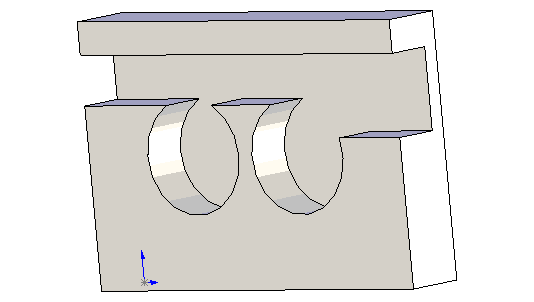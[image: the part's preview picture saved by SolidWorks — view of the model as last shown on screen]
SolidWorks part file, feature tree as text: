
SOLIDWORKS PART (.sldprt)
format: sldprt  version: not decoded by parser v0  size: 99,328 bytes
history: native  units: mm
features: sketch x4, cut_extrude x3, extrude x1 (+11 scaffold rows collapsed)
feature tree (19):
  scaffold x11  (default folders/planes/origin — collapsed)
  sketch  "Sketch1"  dims[D1=50.8mm D2=76.2mm D3=~26.148107mm]
  extrude  "Extrude1"  Depth=12.7mm
  sketch  "Sketch2"  dims[D1=9.525mm D2=6.35mm D3=12.7mm D4=3.175mm]
  cut_extrude  "Cut-Extrude1"  [1 undecoded]
  sketch  "Sketch3"  dims[D1=22.225mm D2=22.225mm D3=25.4mm D4=25.4mm]
  cut_extrude  "Cut-Extrude2"  Depth=9.525mm
  sketch  "Sketch4"  dims[D1=6.35mm D2=9.525mm]
  cut_extrude  "Cut-Extrude3"  [1 undecoded]
decode coverage: 6 of 8 modeling features carry decoded parameters
note: ~ marks probable driven/reference dimensions
note: 2 parameter values undecoded
note: suppression state not decoded; provenance and decode notes live in map.json
